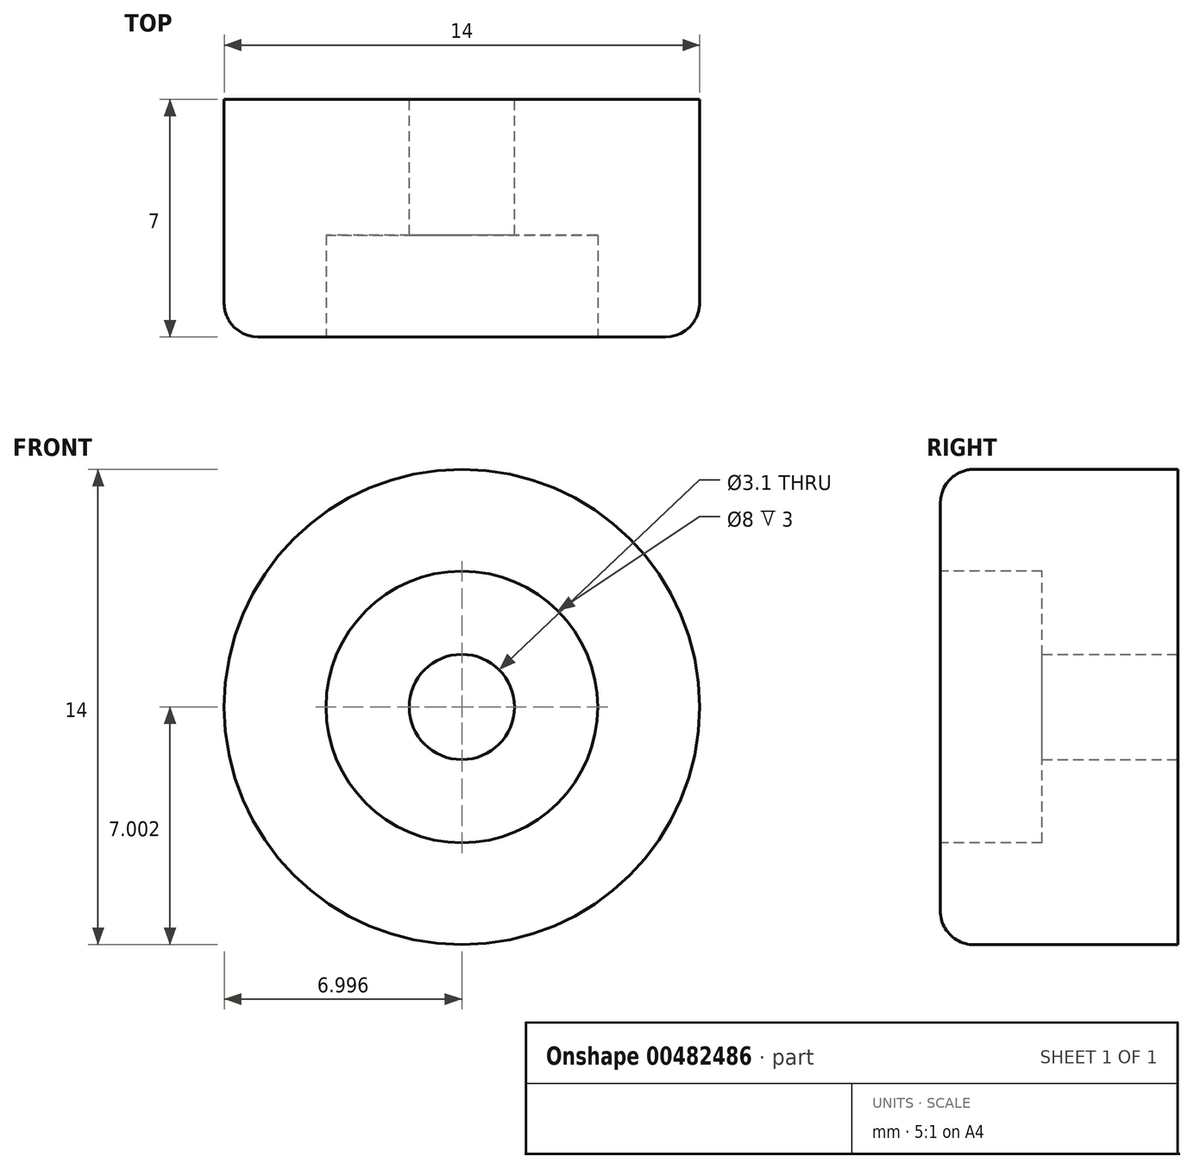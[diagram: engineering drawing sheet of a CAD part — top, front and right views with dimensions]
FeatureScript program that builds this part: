
annotation { "Feature Type Name" : "Feature", "Feature Type Description" : "" }
export const myFeature = defineFeature(function(context is Context, id is Id, definition is map)
    precondition{}
    {
        {
            var Q0;
            Q0=qCreatedBy(makeId("Front.planeOp"),FACE);
            var sketch = newSketch(context, id + "F0", { "sketchPlane" : qUnion([Q0])});
            skCircle(sketch, "E0", {"center": v(-31.37, 43.22) * mm, "radius": 7 * mm});
            skCircle(sketch, "E1", {"center": v(-31.37, 43.22) * mm, "radius": 1.55 * mm});
            skSolve(sketch);
        }
        {
            var Q0;
            Q0=makeQuery(id+"F0.imprint","IMPRINT",FACE,{"disambiguationData":[TD([[makeQuery(id+"F0.imprint","IMPRINT",EDGE,{"derivedFrom":sQuery(id+"F0.wireOp",EDGE,"E0")}),1.0]])]});
            extrude(context, id + "F1", {"entities" : qUnion([Q0]), "depth" : 7 * mm, "offsetDistance" : 25 * mm});
        }
        {
            var Q0;
            Q0=makeQuery(id+"F1.opExtrude","CAP_EDGE",EDGE,{"disambiguationData":[OSD([sQuery(id+"F0.wireOp",EDGE,"E0")])],"isStart":false});
            fillet(context, id + "F2", {"entities" : qUnion([Q0]), "radius" : 1 * mm, "tangentPropagation" : true, "allowEdgeOverflow" : false});
        }
        {
            var Q0;
            Q0=makeQuery(id+"F1.opExtrude","CAP_FACE",FACE,{"disambiguationData":[OSD([sQuery(id+"F0.wireOp",EDGE,"E0"),sQuery(id+"F0.wireOp",EDGE,"E1")])],"isStart":false});
            var sketch = newSketch(context, id + "F3", { "sketchPlane" : qUnion([Q0])});
            skCircle(sketch, "E2", {"center": v(-31.37, 43.22) * mm, "radius": 4 * mm});
            skSolve(sketch);
        }
        {
            var Q0;
            Q0 = qSketchRegion(id + "F3", true);
            extrude(context, id + "F4", {"entities" : qUnion([Q0]), "operationType" : NewBodyOperationType.REMOVE, "oppositeDirection" : true, "depth" : 3 * mm, "offsetDistance" : 25 * mm});
        }
    });
